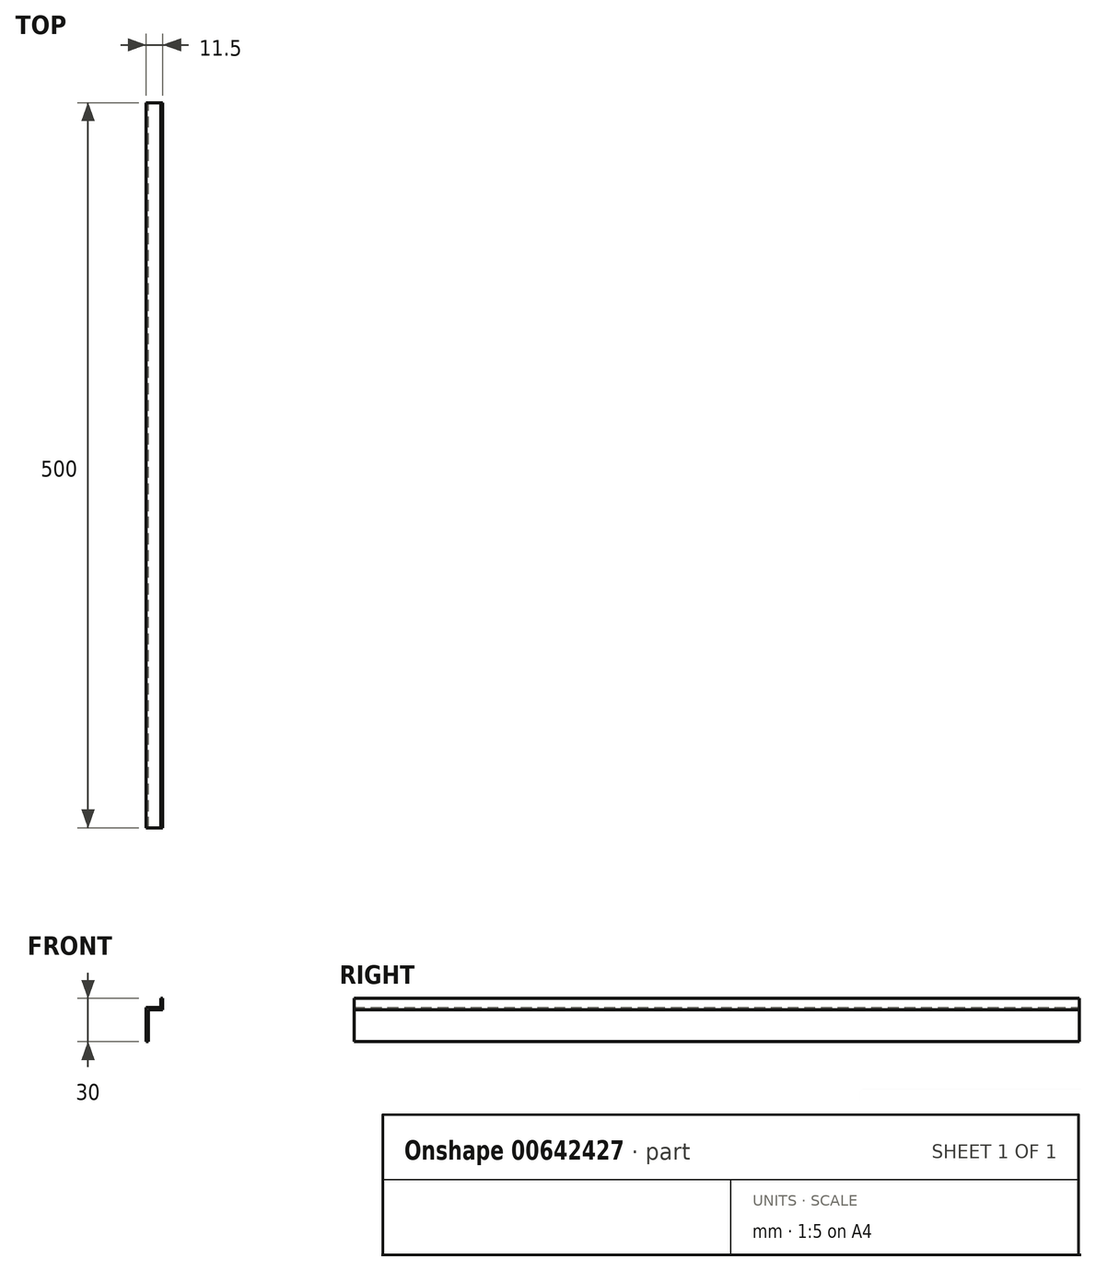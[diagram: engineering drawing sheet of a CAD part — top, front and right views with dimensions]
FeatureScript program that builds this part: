
annotation { "Feature Type Name" : "Feature", "Feature Type Description" : "" }
export const myFeature = defineFeature(function(context is Context, id is Id, definition is map)
    precondition{}
    {
        {
            var Q0;
            Q0=qCreatedBy(makeId("Front.planeOp"),FACE);
            var sketch = newSketch(context, id + "F0", { "sketchPlane" : qUnion([Q0])});
            skLineSegment(sketch, "E0", {"start": v(-28.34, 49.15) * mm, "end": v(-28.34, 41.15) * mm});
            skLineSegment(sketch, "E1", {"start": v(-28.34, 41.15) * mm, "end": v(-38.34, 41.15) * mm});
            skLineSegment(sketch, "E2", {"start": v(-38.34, 41.15) * mm, "end": v(-38.34, 19.15) * mm});
            skLineSegment(sketch, "E3", {"start": v(-28.34, 49.15) * mm, "end": v(-29.84, 49.15) * mm});
            skLineSegment(sketch, "E4", {"start": v(-29.84, 49.15) * mm, "end": v(-29.84, 42.65) * mm});
            skLineSegment(sketch, "E5", {"start": v(-29.84, 42.65) * mm, "end": v(-39.84, 42.65) * mm});
            skLineSegment(sketch, "E6", {"start": v(-39.84, 42.65) * mm, "end": v(-39.84, 19.15) * mm});
            skLineSegment(sketch, "E7", {"start": v(-39.84, 19.15) * mm, "end": v(-38.34, 19.15) * mm});
            skSolve(sketch);
        }
        {
            var Q0;
            Q0=makeQuery(id+"F0.imprint","IMPRINT",FACE,{"disambiguationData":[TD([[makeQuery(id+"F0.imprint","IMPRINT",EDGE,{"derivedFrom":sQuery(id+"F0.wireOp",EDGE,"E0")}),-1.0]])]});
            extrude(context, id + "F1", {"entities" : qUnion([Q0]), "depth" : 500 * mm, "offsetDistance" : 25 * mm});
        }
    });
